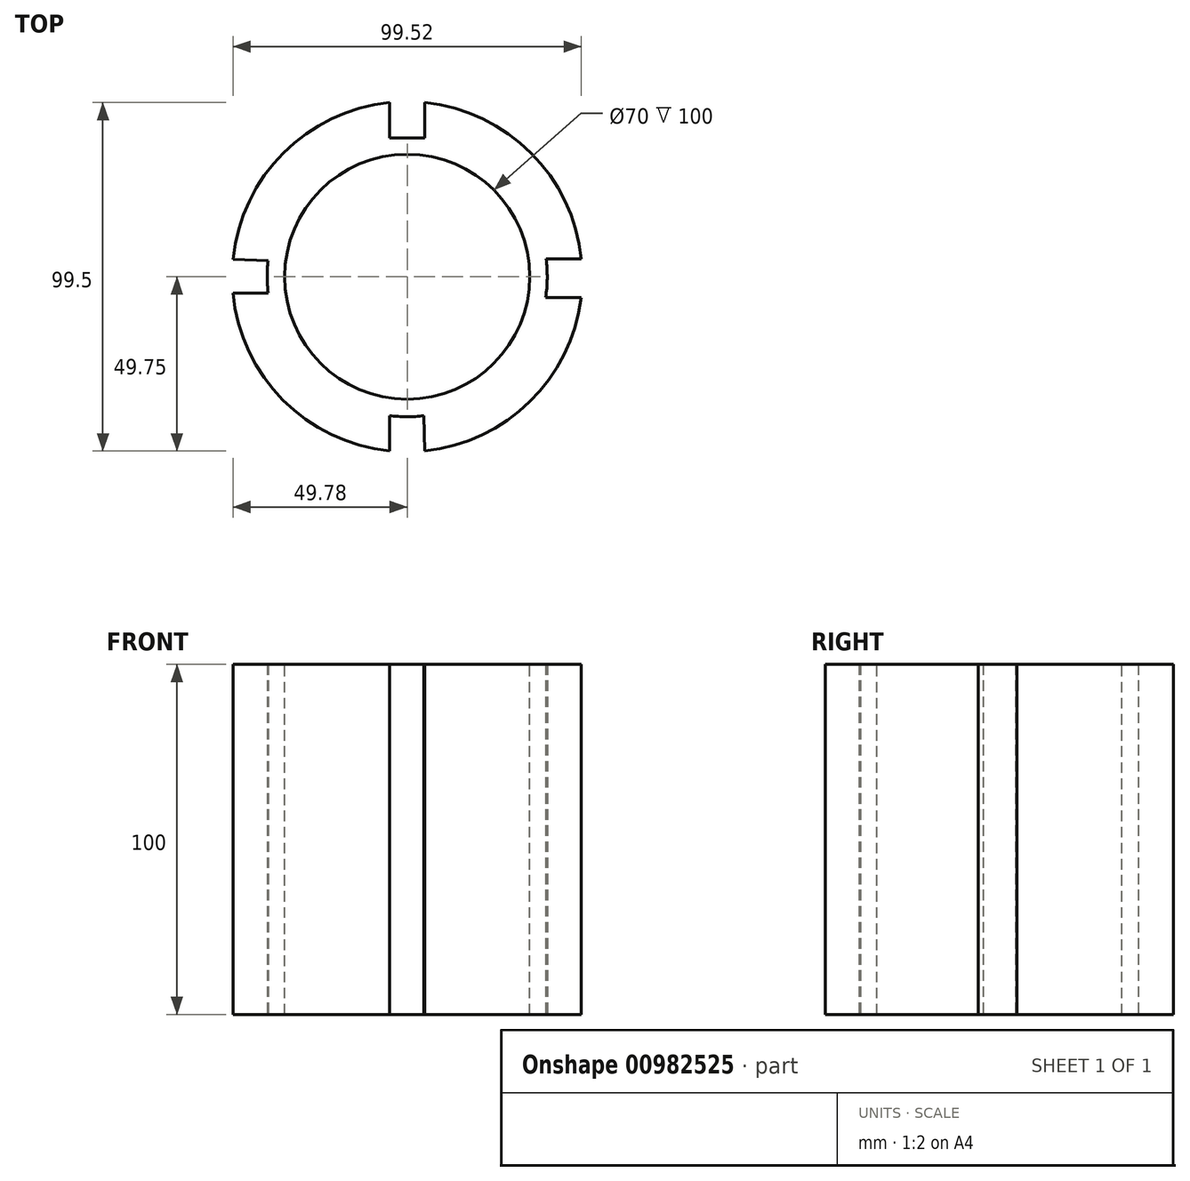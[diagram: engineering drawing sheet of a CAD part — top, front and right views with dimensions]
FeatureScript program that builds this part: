
annotation { "Feature Type Name" : "Feature", "Feature Type Description" : "" }
export const myFeature = defineFeature(function(context is Context, id is Id, definition is map)
    precondition{}
    {
        {
            var Q0;
            Q0=qCreatedBy(makeId("Top.planeOp"),FACE);
            var sketch = newSketch(context, id + "F0", { "sketchPlane" : qUnion([Q0])});
            skArc(sketch, "E0", {"start": v(-5, 39.69) * mm, "mid": v(0, -40) * mm, "end": v(5, 39.69) * mm});
            skArc(sketch, "E1", {"start": v(-5, 49.75) * mm, "mid": v(-35.36, 35.36) * mm, "end": v(-49.75, 5) * mm});
            skLineSegment(sketch, "E2.bottom", {"start": v(-5, 39.69) * mm, "end": v(5, 39.69) * mm});
            skLineSegment(sketch, "E2.left", {"start": v(-5, 39.69) * mm, "end": v(-5, 49.75) * mm});
            skLineSegment(sketch, "E2.right", {"start": v(5, 39.69) * mm, "end": v(5, 49.75) * mm});
            skLineSegment(sketch, "E3.1.0", {"start": v(39.55, -5.99) * mm, "end": v(49.64, -5.99) * mm});
            skLineSegment(sketch, "E3.1.1", {"start": v(39.68, 5.08) * mm, "end": v(49.74, 5.08) * mm});
            skLineSegment(sketch, "E3.2.0", {"start": v(-5.08, -39.68) * mm, "end": v(-5, -49.75) * mm});
            skLineSegment(sketch, "E3.2.1", {"start": v(4.8, -39.71) * mm, "end": v(5, -49.75) * mm});
            skLineSegment(sketch, "E3.3.0", {"start": v(-39.74, 4.6) * mm, "end": v(-49.75, 5) * mm});
            skLineSegment(sketch, "E3.3.1", {"start": v(-39.73, -4.66) * mm, "end": v(-49.78, -4.66) * mm});
            skPoint(sketch, "E3.center", {"position": v(-0.43, -0.7) * mm});
            skLineSegment(sketch, "E3.anchor1", {"start": v(-0.43, -0.7) * mm, "end": v(5, 39.69) * mm, "construction": true});
            skLineSegment(sketch, "E3.anchor2", {"start": v(-0.43, -0.7) * mm, "end": v(-39.74, 4.6) * mm, "construction": true});
            skArc(sketch, "E4.trimOffspring", {"start": v(49.74, 5.08) * mm, "mid": v(35.33, 35.38) * mm, "end": v(5, 49.75) * mm});
            skArc(sketch, "E5.trimOffspring", {"start": v(5, -49.75) * mm, "mid": v(35, -35.7) * mm, "end": v(49.64, -5.99) * mm});
            skArc(sketch, "E6.trimOffspring", {"start": v(-49.78, -4.66) * mm, "mid": v(-35.48, -35.23) * mm, "end": v(-5, -49.75) * mm});
            skSolve(sketch);
        }
        {
            var Q0;
            Q0 = qSketchRegion(id + "F0", true);
            extrude(context, id + "F1", {"entities" : qUnion([Q0]), "endBound" : BoundingType.SYMMETRIC, "depth" : 100 * mm, "offsetDistance" : 25 * mm});
        }
        {
            var Q0;
            Q0=makeQuery(id+"F1.opExtrude","CAP_FACE",FACE,{"disambiguationData":[OSD([sQuery(id+"F0.wireOp",EDGE,"E0"),sQuery(id+"F0.wireOp",EDGE,"E1"),sQuery(id+"F0.wireOp",EDGE,"E2.bottom"),sQuery(id+"F0.wireOp",EDGE,"E2.left"),sQuery(id+"F0.wireOp",EDGE,"E2.right"),sQuery(id+"F0.wireOp",EDGE,"E3.1.0"),sQuery(id+"F0.wireOp",EDGE,"E3.1.1"),sQuery(id+"F0.wireOp",EDGE,"E3.2.0"),sQuery(id+"F0.wireOp",EDGE,"E3.2.1"),sQuery(id+"F0.wireOp",EDGE,"E3.3.0"),sQuery(id+"F0.wireOp",EDGE,"E3.3.1"),sQuery(id+"F0.wireOp",EDGE,"E4.trimOffspring"),sQuery(id+"F0.wireOp",EDGE,"E5.trimOffspring"),sQuery(id+"F0.wireOp",EDGE,"E6.trimOffspring")])],"isStart":false});
            var sketch = newSketch(context, id + "F2", { "sketchPlane" : qUnion([Q0])});
            skCircle(sketch, "E7", {"center": v(0, 0) * mm, "radius": 35 * mm});
            skSolve(sketch);
        }
        {
            var Q0;
            Q0=makeQuery(id+"F2.imprint","IMPRINT",FACE,{"disambiguationData":[TD([[makeQuery(id+"F2.imprint","IMPRINT",EDGE,{"derivedFrom":sQuery(id+"F2.wireOp",EDGE,"E7")}),1.0]])]});
            extrude(context, id + "F3", {"entities" : qUnion([Q0]), "operationType" : NewBodyOperationType.REMOVE, "oppositeDirection" : true, "depth" : 200 * mm, "offsetDistance" : 25 * mm});
        }
    });
